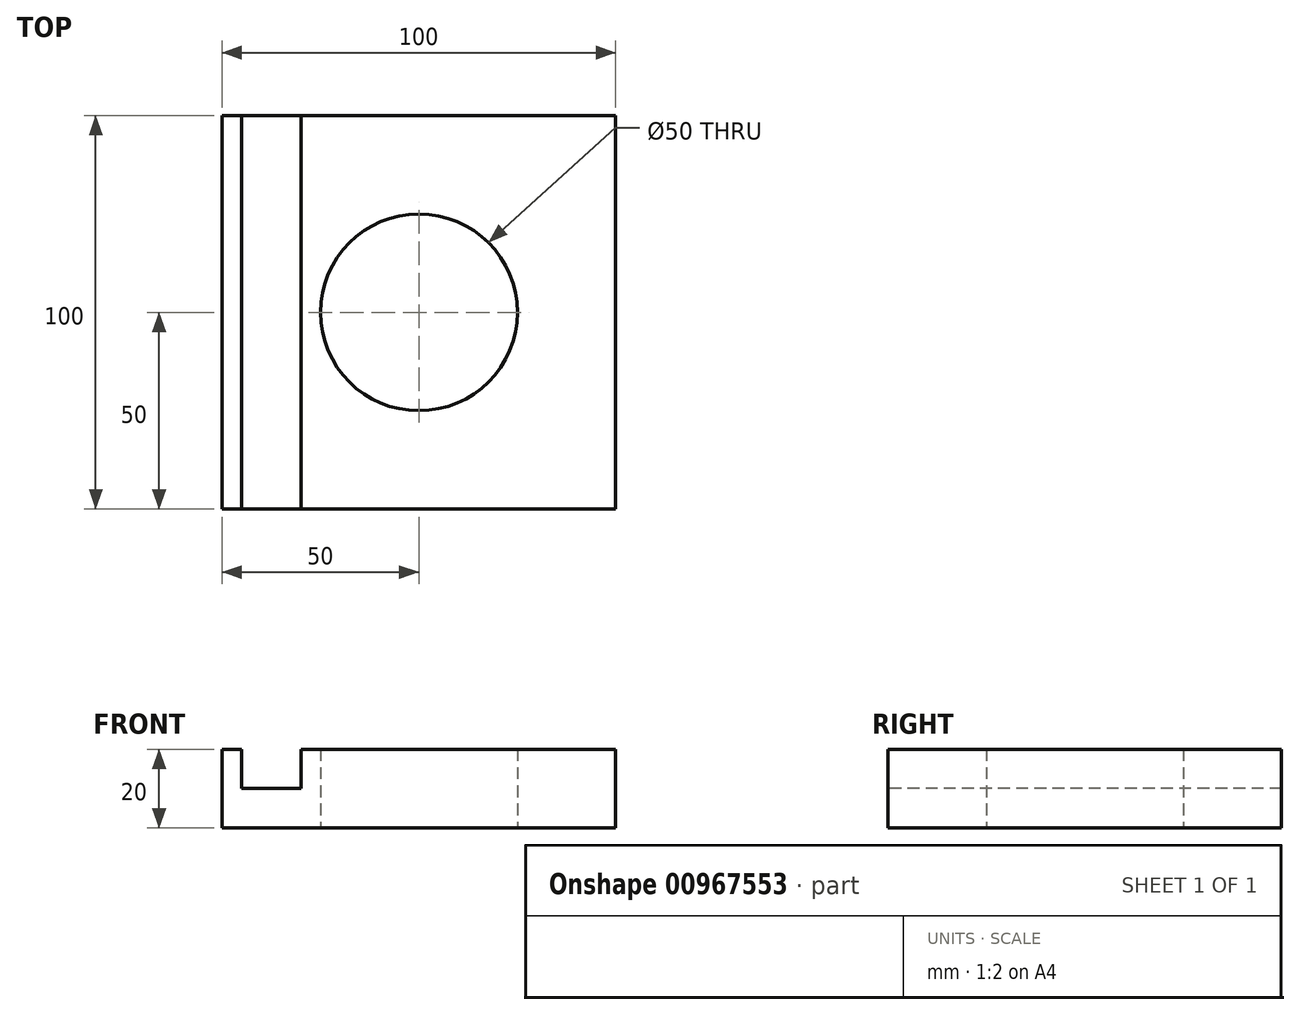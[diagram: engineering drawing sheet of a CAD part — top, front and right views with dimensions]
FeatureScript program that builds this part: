
annotation { "Feature Type Name" : "Feature", "Feature Type Description" : "" }
export const myFeature = defineFeature(function(context is Context, id is Id, definition is map)
    precondition{}
    {
        {
            var Q0;
            Q0=qCreatedBy(makeId("Top.planeOp"),FACE);
            var sketch = newSketch(context, id + "F0", { "sketchPlane" : qUnion([Q0])});
            skLineSegment(sketch, "E0.bottom", {"start": v(50, 50) * mm, "end": v(-50, 50) * mm});
            skLineSegment(sketch, "E0.top", {"start": v(50, -50) * mm, "end": v(-50, -50) * mm});
            skLineSegment(sketch, "E0.left", {"start": v(50, 50) * mm, "end": v(50, -50) * mm});
            skLineSegment(sketch, "E0.right", {"start": v(-50, 50) * mm, "end": v(-50, -50) * mm});
            skPoint(sketch, "E0.middle", {"position": v(0, 0) * mm});
            skSolve(sketch);
        }
        {
            var Q0;
            Q0=makeQuery(id+"F0.imprint","IMPRINT",FACE,{"disambiguationData":[TD([[makeQuery(id+"F0.imprint","IMPRINT",EDGE,{"derivedFrom":sQuery(id+"F0.wireOp",EDGE,"E0.bottom")}),1.0]])]});
            var sketch = newSketch(context, id + "F1", { "sketchPlane" : qUnion([Q0])});
            skCircle(sketch, "E1", {"center": v(0, 0) * mm, "radius": 25 * mm});
            skSolve(sketch);
        }
        {
            var Q0;
            Q0=makeQuery(id+"F1.imprint","IMPRINT",FACE,{"disambiguationData":[TD([[makeQuery(id+"F1.imprint","IMPRINT",EDGE,{"derivedFrom":sQuery(id+"F1.wireOp",EDGE,"E1")}),-1.0]])]});
            var Q1;
            Q1=sQuery(id+"F0.wireOp",EDGE,"E0.left");
            var Q2;
            Q2=sQuery(id+"F0.wireOp",EDGE,"E0.bottom");
            var Q3;
            Q3=sQuery(id+"F0.wireOp",EDGE,"E0.top");
            var Q4;
            Q4=sQuery(id+"F0.wireOp",EDGE,"E0.right");
            var Q5;
            Q5=sQuery(id+"F1.wireOp",EDGE,"E1");
            extrude(context, id + "F2", {"entities" : qUnion([Q0]), "surfaceEntities" : qUnion([Q1, Q2, Q3, Q4, Q5]), "depth" : 20 * mm, "offsetDistance" : 25 * mm});
        }
        {
            var Q0;
            Q0=makeQuery(id+"F2.opExtrude","CAP_FACE",FACE,{"disambiguationData":[OSD([sQuery(id+"F0.wireOp",EDGE,"E0.bottom"),sQuery(id+"F0.wireOp",EDGE,"E0.top"),sQuery(id+"F0.wireOp",EDGE,"E0.left"),sQuery(id+"F0.wireOp",EDGE,"E0.right"),sQuery(id+"F1.wireOp",EDGE,"E1")])],"isStart":false});
            var sketch = newSketch(context, id + "F3", { "sketchPlane" : qUnion([Q0])});
            skLineSegment(sketch, "E2.bottom", {"start": v(-45, 50) * mm, "end": v(-30, 50) * mm});
            skLineSegment(sketch, "E2.top", {"start": v(-45, -50) * mm, "end": v(-30, -50) * mm});
            skLineSegment(sketch, "E2.left", {"start": v(-45, 50) * mm, "end": v(-45, -50) * mm});
            skLineSegment(sketch, "E2.right", {"start": v(-30, 50) * mm, "end": v(-30, -50) * mm});
            skPoint(sketch, "E2.middle", {"position": v(-37.5, 0) * mm});
            skSolve(sketch);
        }
        {
            var Q0;
            Q0=makeQuery(id+"F3.imprint","IMPRINT",FACE,{"disambiguationData":[TD([[makeQuery(id+"F3.imprint","IMPRINT",EDGE,{"derivedFrom":sQuery(id+"F3.wireOp",EDGE,"E2.bottom")}),1.0]])]});
            extrude(context, id + "F4", {"entities" : qUnion([Q0]), "operationType" : NewBodyOperationType.REMOVE, "oppositeDirection" : true, "depth" : 10 * mm, "offsetDistance" : 25 * mm});
        }
    });
